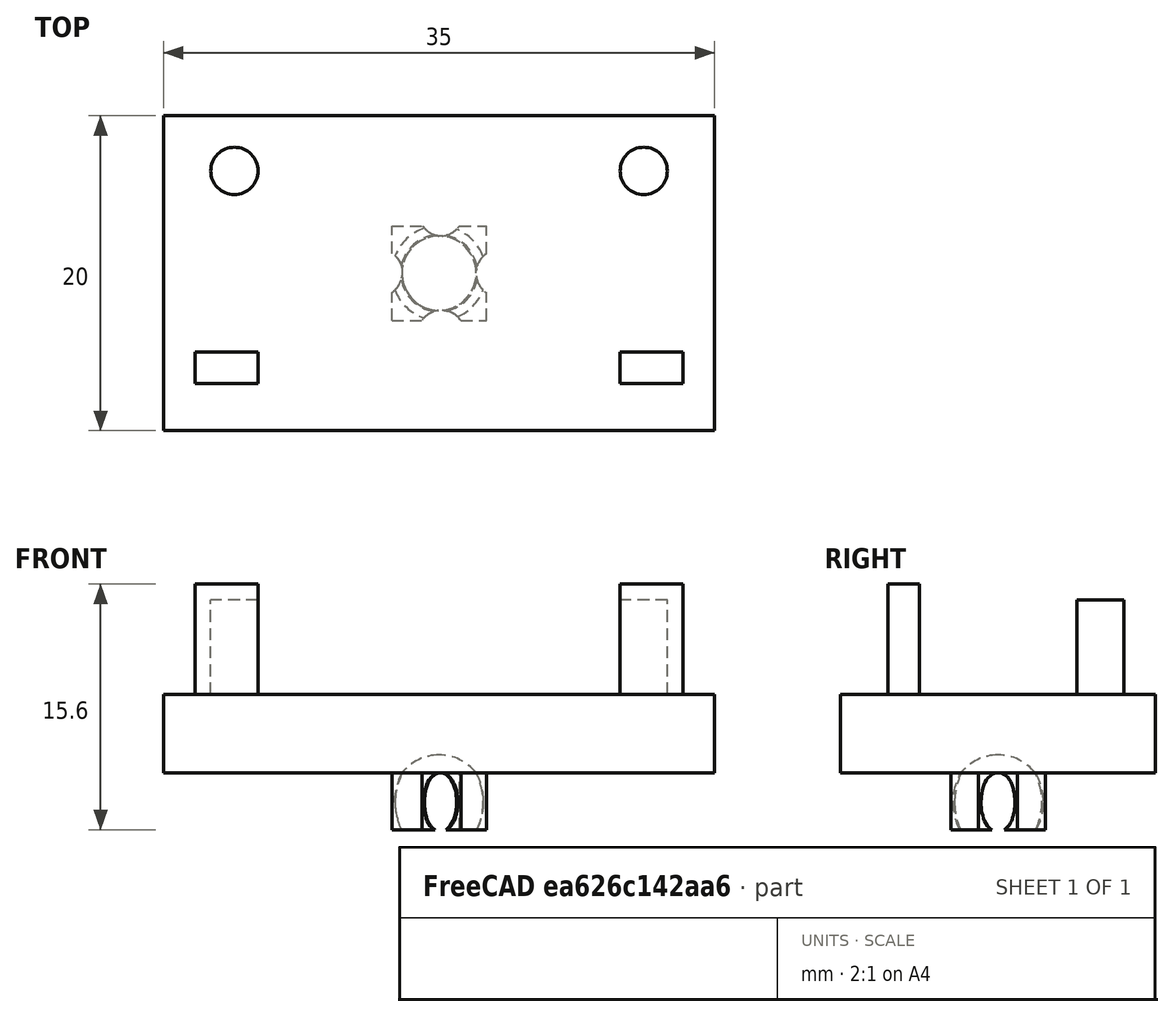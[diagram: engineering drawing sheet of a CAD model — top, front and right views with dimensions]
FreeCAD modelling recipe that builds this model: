
FCSTD DOCUMENT  (FreeCAD 0.19R24276 (Git))
Label: modelisation support bille
License: All rights reserved
LicenseURL: http://en.wikipedia.org/wiki/All_rights_reserved
objects: Part::FeaturePython×21, Part::Cylinder×17, Part::Box×8, Part::Sphere×5, App::MeasureDistance×2
note: 51 computed .brp shape members not serialized (recipe doc carries the construction recipe); baked Part::Feature solids carry a one-line shape summary decoded from their .brp

FEATURE [Part::Box] Box  label="Cube"
  AttacherType = Attacher::AttachEngine3D
  Height = 5
  Length = 35
  Width = 20
FEATURE [Part::Box] Box001  label="Cube001"
  AttacherType = Attacher::AttachEngine3D
  Height = 7
  Length = 2
  Placement = pos=(6,3,5) rot=(0,0,1;1.5708rad)
  Width = 4
FEATURE [Part::Box] Box002  label="Cube002"
  AttacherType = Attacher::AttachEngine3D
  Height = 7
  Length = 2
  Placement = pos=(33,3,5) rot=(0,0,1;1.5708rad)
  Width = 4
FEATURE [Part::Cylinder] Cylinder  label="Cylindre"
  Angle = 360
  AttacherType = Attacher::AttachEngine3D
  Height = 6
  Placement = pos=(4.5,16.5,5) rot=(0,0,1;0rad)
  Radius = 1.5
FEATURE [App::MeasureDistance] Distance  label="Distance: 1,09 mm"
  Distance = 1.08718
  P1 = (4.1635,18.958,5.02402)
  P2 = (3.85439,20,5)
FEATURE [App::MeasureDistance] Distance001  label="Distance: 2,03 mm"
  Distance = 2.02896
  P1 = (4.28672,17.9847,5.03333)
  P2 = (4.05363,20,5)
FEATURE [Part::Cylinder] Cylinder001  label="Cylindre001"
  Angle = 360
  AttacherType = Attacher::AttachEngine3D
  Height = 6
  Placement = pos=(30.5,16.5,5) rot=(0,0,1;0rad)
  Radius = 1.5
FEATURE [Part::Sphere] Sphere  label="Sphère"
  Angle1 = -90
  Angle2 = 90
  Angle3 = 360
  AttacherType = Attacher::AttachEngine3D
  Placement = pos=(17.5,10,-1.85) rot=(0,0,1;0rad)
  Radius = 3
FEATURE [Part::Box] Box003  label="Cube003"
  AttacherType = Attacher::AttachEngine3D
  Height = 3.6
  Length = 6
  Placement = pos=(14.5,7,-3.6) rot=(0,0,1;0rad)
  Width = 6
FEATURE [Part::Sphere] Sphere001  label="Sphère001"
  Angle1 = -90
  Angle2 = 90
  Angle3 = 360
  AttacherType = Attacher::AttachEngine3D
  Placement = pos=(17.5,10,-1.85) rot=(0,0,1;0rad)
  Radius = 3
FEATURE [Part::FeaturePython] Cutout  # WARN: FeaturePython — macro-defined, semantics opaque (R4)
  Base = -> Box003
  Tolerance = 0
  Tool = -> Sphere
FEATURE [Part::FeaturePython] Cutout001  # WARN: FeaturePython — macro-defined, semantics opaque (R4)
  Base = -> Box
  Tolerance = 0
  Tool = -> Sphere001
FEATURE [Part::Cylinder] Cylinder002  label="Cylindre002"
  Angle = 360
  AttacherType = Attacher::AttachEngine3D
  Height = 5
  Placement = pos=(13.65,10,-5) rot=(0,0,1;0rad)
  Radius = 1.5
FEATURE [Part::Cylinder] Cylinder003  label="Cylindre003"
  Angle = 360
  AttacherType = Attacher::AttachEngine3D
  Height = 5
  Placement = pos=(21.35,10,-5) rot=(0,0,1;0rad)
  Radius = 1.5
FEATURE [Part::Cylinder] Cylinder004  label="Cylindre004"
  Angle = 360
  AttacherType = Attacher::AttachEngine3D
  Height = 5
  Placement = pos=(17.65,6.15,-5) rot=(0,0,1;0rad)
  Radius = 1.5
FEATURE [Part::Cylinder] Cylinder005  label="Cylindre005"
  Angle = 360
  AttacherType = Attacher::AttachEngine3D
  Height = 5
  Placement = pos=(17.55,13.85,-5) rot=(0,0,1;0rad)
  Radius = 1.5
FEATURE [Part::Box] Box004  label="Cube004"
  AttacherType = Attacher::AttachEngine3D
  Height = 3.6
  Length = 6
  Placement = pos=(14.5,7,-3.6) rot=(0,0,1;0rad)
  Width = 6
FEATURE [Part::Cylinder] Cylinder006  label="Cylindre006"
  Angle = 360
  AttacherType = Attacher::AttachEngine3D
  Height = 5
  Placement = pos=(13.65,10,-5) rot=(0,0,1;0rad)
  Radius = 1.5
FEATURE [Part::Sphere] Sphere002  label="Sphère002"
  Angle1 = -90
  Angle2 = 90
  Angle3 = 360
  AttacherType = Attacher::AttachEngine3D
  Placement = pos=(17.5,10,-1.85) rot=(0,0,1;0rad)
  Radius = 3
FEATURE [Part::FeaturePython] Cutout003  # WARN: FeaturePython — macro-defined, semantics opaque (R4)
  Base = -> Box004
  Tolerance = 0
  Tool = -> Sphere002
FEATURE [Part::FeaturePython] Cutout004  # WARN: FeaturePython — macro-defined, semantics opaque (R4)
  Base = -> Cutout003
  Tolerance = 0
  Tool = -> Cylinder006
FEATURE [Part::FeaturePython] Cutout005  # WARN: FeaturePython — macro-defined, semantics opaque (R4)
  Base = -> Cutout004
  Tolerance = 0
  Tool = -> Cylinder003
FEATURE [Part::FeaturePython] Cutout006  label="coté gauche bas"  # WARN: FeaturePython — macro-defined, semantics opaque (R4)
  Base = -> Cutout005
  Tolerance = 0
  Tool = -> Cylinder004
FEATURE [Part::Sphere] Sphere003  label="Sphère003"
  Angle1 = -90
  Angle2 = 90
  Angle3 = 360
  AttacherType = Attacher::AttachEngine3D
  Placement = pos=(17.5,10,-1.85) rot=(0,0,1;0rad)
  Radius = 3
FEATURE [Part::Box] Box005  label="Cube005"
  AttacherType = Attacher::AttachEngine3D
  Height = 3.6
  Length = 6
  Placement = pos=(14.5,7,-3.6) rot=(0,0,1;0rad)
  Width = 6
FEATURE [Part::FeaturePython] Cutout007  # WARN: FeaturePython — macro-defined, semantics opaque (R4)
  Base = -> Box005
  Tolerance = 0
  Tool = -> Sphere003
FEATURE [Part::Sphere] Sphere004  label="Sphère004"
  Angle1 = -90
  Angle2 = 90
  Angle3 = 360
  AttacherType = Attacher::AttachEngine3D
  Placement = pos=(17.5,10,-1.85) rot=(0,0,1;0rad)
  Radius = 3
FEATURE [Part::Box] Box006  label="Cube006"
  AttacherType = Attacher::AttachEngine3D
  Height = 3.6
  Length = 6
  Placement = pos=(14.5,7,-3.6) rot=(0,0,1;0rad)
  Width = 6
FEATURE [Part::FeaturePython] Cutout008  # WARN: FeaturePython — macro-defined, semantics opaque (R4)
  Base = -> Box006
  Tolerance = 0
  Tool = -> Sphere004
FEATURE [Part::FeaturePython] Cutout009  # WARN: FeaturePython — macro-defined, semantics opaque (R4)
  Base = -> Cutout
  Tolerance = 0
  Tool = -> Cylinder002
FEATURE [Part::FeaturePython] Cutout010  # WARN: FeaturePython — macro-defined, semantics opaque (R4)
  Base = -> Cutout009
  Tolerance = 0
  Tool = -> Cylinder005
FEATURE [Part::Cylinder] Cylinder007  label="Cylindre007"
  Angle = 360
  AttacherType = Attacher::AttachEngine3D
  Height = 5
  Placement = pos=(17.65,6.2,-5) rot=(0,0,1;0rad)
  Radius = 1.5
FEATURE [Part::FeaturePython] Cutout011  # WARN: FeaturePython — macro-defined, semantics opaque (R4)
  Base = -> Cutout010
  Tolerance = 0
  Tool = -> Cylinder007
FEATURE [Part::Cylinder] Cylinder008  label="Cylindre008"
  Angle = 360
  AttacherType = Attacher::AttachEngine3D
  Height = 5
  Placement = pos=(21.35,10,-5) rot=(0,0,1;0rad)
  Radius = 1.5
FEATURE [Part::FeaturePython] Cutout012  label="coté droite haut"  # WARN: FeaturePython — macro-defined, semantics opaque (R4)
  Base = -> Cutout011
  Tolerance = 0
  Tool = -> Cylinder008
FEATURE [Part::Cylinder] Cylinder009  label="Cylindre009"
  Angle = 360
  AttacherType = Attacher::AttachEngine3D
  Height = 5
  Placement = pos=(21.35,10,-5) rot=(0,0,1;0rad)
  Radius = 1.5
FEATURE [Part::FeaturePython] Cutout013  # WARN: FeaturePython — macro-defined, semantics opaque (R4)
  Base = -> Cutout007
  Tolerance = 0
  Tool = -> Cylinder009
FEATURE [Part::Cylinder] Cylinder010  label="Cylindre010"
  Angle = 360
  AttacherType = Attacher::AttachEngine3D
  Height = 5
  Placement = pos=(17.7,13.85,-5) rot=(0,0,1;0rad)
  Radius = 1.5
FEATURE [Part::FeaturePython] Cutout014  # WARN: FeaturePython — macro-defined, semantics opaque (R4)
  Base = -> Cutout013
  Tolerance = 0
  Tool = -> Cylinder010
FEATURE [Part::Cylinder] Cylinder011  label="Cylindre011"
  Angle = 360
  AttacherType = Attacher::AttachEngine3D
  Height = 5
  Placement = pos=(17.65,6.15,-5) rot=(0,0,1;0rad)
  Radius = 1.5
FEATURE [Part::FeaturePython] Cutout015  # WARN: FeaturePython — macro-defined, semantics opaque (R4)
  Base = -> Cutout014
  Tolerance = 0
  Tool = -> Cylinder011
FEATURE [Part::Cylinder] Cylinder012  label="Cylindre012"
  Angle = 360
  AttacherType = Attacher::AttachEngine3D
  Height = 5
  Placement = pos=(13.7,10,-5) rot=(0,0,1;0rad)
  Radius = 1.5
FEATURE [Part::FeaturePython] Cutout016  label="coté droit bas"  # WARN: FeaturePython — macro-defined, semantics opaque (R4)
  Base = -> Cutout015
  Tolerance = 0
  Tool = -> Cylinder012
FEATURE [Part::Cylinder] Cylinder013  label="Cylindre013"
  Angle = 360
  AttacherType = Attacher::AttachEngine3D
  Height = 5
  Placement = pos=(17.625,13.85,-5) rot=(0,0,1;0rad)
  Radius = 1.5
FEATURE [Part::Cylinder] Cylinder014  label="Cylindre014"
  Angle = 360
  AttacherType = Attacher::AttachEngine3D
  Height = 5
  Placement = pos=(13.7,10.025,-5) rot=(0,0,1;0rad)
  Radius = 1.5
FEATURE [Part::Cylinder] Cylinder015  label="Cylindre015"
  Angle = 360
  AttacherType = Attacher::AttachEngine3D
  Height = 5
  Placement = pos=(21.35,10,-5) rot=(0,0,1;0rad)
  Radius = 1.5
FEATURE [Part::FeaturePython] Cutout017  # WARN: FeaturePython — macro-defined, semantics opaque (R4)
  Base = -> Cutout008
  Tolerance = 0
  Tool = -> Cylinder014
FEATURE [Part::FeaturePython] Cutout018  # WARN: FeaturePython — macro-defined, semantics opaque (R4)
  Base = -> Cutout017
  Tolerance = 0
  Tool = -> Cylinder013
FEATURE [Part::FeaturePython] Cutout019  # WARN: FeaturePython — macro-defined, semantics opaque (R4)
  Base = -> Cutout018
  Tolerance = 0
  Tool = -> Cylinder015
FEATURE [Part::Cylinder] Cylinder016  label="Cylindre016"
  Angle = 360
  AttacherType = Attacher::AttachEngine3D
  Height = 5
  Placement = pos=(17.65,6.15,-5) rot=(0,0,1;0rad)
  Radius = 1.5
FEATURE [Part::Box] Box007  label="Cube007"
  AttacherType = Attacher::AttachEngine3D
  Height = 15
  Length = 5
  Placement = pos=(10.355,3,-11.68) rot=(0,0,1;0rad)
  Width = 5
FEATURE [Part::FeaturePython] Cutout020  # WARN: FeaturePython — macro-defined, semantics opaque (R4)
  Base = -> Cutout019
  Tolerance = 0
  Tool = -> Box007
FEATURE [Part::FeaturePython] Cutout021  label="coté gauche en haut"  # WARN: FeaturePython — macro-defined, semantics opaque (R4)
  Base = -> Cutout020
  Tolerance = 0
  Tool = -> Cylinder016
